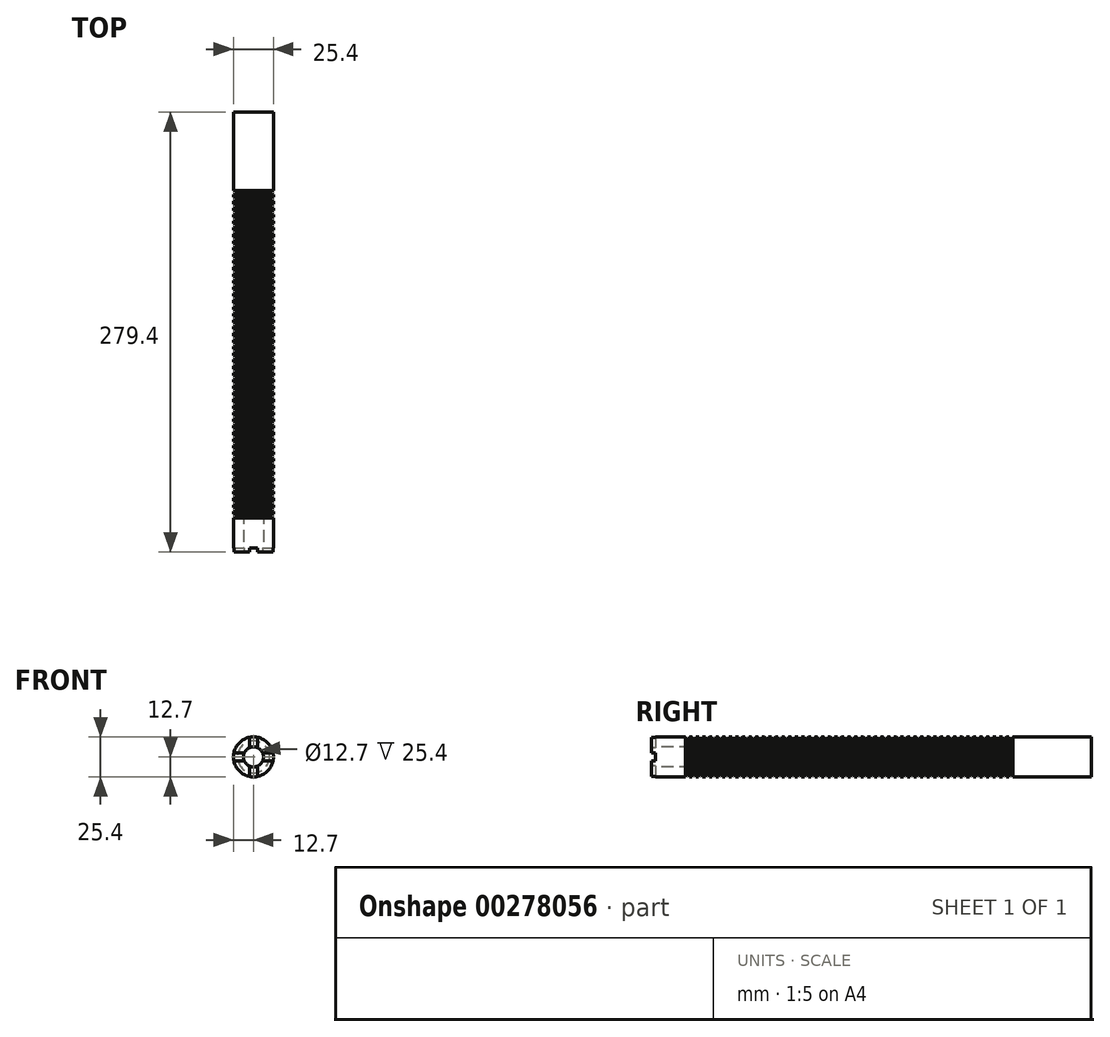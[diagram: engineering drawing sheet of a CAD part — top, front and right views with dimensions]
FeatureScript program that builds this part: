
annotation { "Feature Type Name" : "Feature", "Feature Type Description" : "" }
export const myFeature = defineFeature(function(context is Context, id is Id, definition is map)
    precondition{}
    {
        {
            var Q0;
            Q0=qCreatedBy(makeId("Front.planeOp"),FACE);
            var sketch = newSketch(context, id + "F0", { "sketchPlane" : qUnion([Q0])});
            skCircle(sketch, "E0", {"center": v(0, 0) * mm, "radius": 12.7 * mm});
            skSolve(sketch);
        }
        {
            var Q0;
            Q0 = qSketchRegion(id + "F0", true);
            extrude(context, id + "F1", {"entities" : qUnion([Q0]), "depth" : 279.4 * mm});
        }
        {
            var Q0;
            Q0=makeQuery(id+"F1.opExtrude","CAP_FACE",FACE,{"disambiguationData":[OSD([sQuery(id+"F0.wireOp",EDGE,"E0")])],"isStart":false});
            var sketch = newSketch(context, id + "F2", { "sketchPlane" : qUnion([Q0])});
            skCircle(sketch, "E1", {"center": v(0, 0) * mm, "radius": 6.35 * mm});
            skSolve(sketch);
        }
        {
            var Q0;
            Q0 = qSketchRegion(id + "F2", true);
            extrude(context, id + "F3", {"entities" : qUnion([Q0]), "operationType" : NewBodyOperationType.REMOVE, "oppositeDirection" : true, "depth" : 25.4 * mm});
        }
        {
            var Q0;
            Q0=makeQuery(id+"F1.opExtrude","CAP_FACE",FACE,{"disambiguationData":[OSD([sQuery(id+"F0.wireOp",EDGE,"E0")])],"isStart":false});
            var sketch = newSketch(context, id + "F4", { "sketchPlane" : qUnion([Q0])});
            skLineSegment(sketch, "E2.bottom", {"start": v(-2.54, 19.05) * mm, "end": v(2.54, 19.05) * mm});
            skLineSegment(sketch, "E2.top", {"start": v(-2.54, -19.05) * mm, "end": v(2.54, -19.05) * mm});
            skLineSegment(sketch, "E2.left", {"start": v(-2.54, 19.05) * mm, "end": v(-2.54, -19.05) * mm});
            skLineSegment(sketch, "E2.right", {"start": v(2.54, 19.05) * mm, "end": v(2.54, -19.05) * mm});
            skSolve(sketch);
        }
        {
            var Q0;
            Q0 = qSketchRegion(id + "F4", true);
            extrude(context, id + "F5", {"entities" : qUnion([Q0]), "operationType" : NewBodyOperationType.REMOVE, "oppositeDirection" : true, "depth" : 2.54 * mm});
        }
        {
            var Q0;
            {var subQ0=sQuery(id+"F0.wireOp",EDGE,"E0");Q0=makeQuery(id+"F5.boolean.opBoolean","SPLIT",FACE,{"disambiguationData":[TD([makeQuery(id+"F5.opExtrude","SWEPT_FACE",FACE,{"disambiguationData":[OSD([sQuery(id+"F4.wireOp",EDGE,"E2.left")])]})])],"derivedFrom":makeQuery(id+"F1.opExtrude","CAP_FACE",FACE,{"disambiguationData":[OSD([subQ0])],"isStart":false})});}
            var sketch = newSketch(context, id + "F6", { "sketchPlane" : qUnion([Q0])});
            skLineSegment(sketch, "E3.bottom", {"start": v(-19.05, 2.54) * mm, "end": v(19.05, 2.54) * mm});
            skLineSegment(sketch, "E3.top", {"start": v(-19.05, -2.54) * mm, "end": v(19.05, -2.54) * mm});
            skLineSegment(sketch, "E3.left", {"start": v(-19.05, 2.54) * mm, "end": v(-19.05, -2.54) * mm});
            skLineSegment(sketch, "E3.right", {"start": v(19.05, 2.54) * mm, "end": v(19.05, -2.54) * mm});
            skSolve(sketch);
        }
        {
            var Q0;
            Q0 = qSketchRegion(id + "F6", true);
            extrude(context, id + "F7", {"entities" : qUnion([Q0]), "operationType" : NewBodyOperationType.REMOVE, "oppositeDirection" : true, "depth" : 2.54 * mm});
        }
        {
            var Q0;
            Q0=qCreatedBy(makeId("Right.planeOp"),FACE);
            var sketch = newSketch(context, id + "F8", { "sketchPlane" : qUnion([Q0])});
            skLineSegment(sketch, "E4", {"start": v(-255.27, 12.7) * mm, "end": v(-257.81, 12.7) * mm});
            skLineSegment(sketch, "E5", {"start": v(-257.8, 12.7) * mm, "end": v(-257.18, 10.16) * mm});
            skLineSegment(sketch, "E6", {"start": v(-257.18, 10.16) * mm, "end": v(-255.9, 10.16) * mm});
            skLineSegment(sketch, "E7", {"start": v(-255.9, 10.16) * mm, "end": v(-255.27, 12.7) * mm});
            skLineSegment(sketch, "E8.1.0.0", {"start": v(-251.71, 10.16) * mm, "end": v(-251.08, 12.7) * mm});
            skLineSegment(sketch, "E8.1.0.1", {"start": v(-253.62, 12.7) * mm, "end": v(-252.98, 10.16) * mm});
            skLineSegment(sketch, "E8.1.0.2", {"start": v(-251.08, 12.7) * mm, "end": v(-253.62, 12.7) * mm});
            skLineSegment(sketch, "E8.1.0.3", {"start": v(-252.98, 10.16) * mm, "end": v(-251.71, 10.16) * mm});
            skLineSegment(sketch, "E8.2.0.0", {"start": v(-247.52, 10.16) * mm, "end": v(-246.89, 12.7) * mm});
            skLineSegment(sketch, "E8.2.0.1", {"start": v(-249.43, 12.7) * mm, "end": v(-248.8, 10.16) * mm});
            skLineSegment(sketch, "E8.2.0.2", {"start": v(-246.89, 12.7) * mm, "end": v(-249.43, 12.7) * mm});
            skLineSegment(sketch, "E8.2.0.3", {"start": v(-248.8, 10.16) * mm, "end": v(-247.52, 10.16) * mm});
            skLineSegment(sketch, "E8.3.0.0", {"start": v(-243.33, 10.16) * mm, "end": v(-242.7, 12.7) * mm});
            skLineSegment(sketch, "E8.3.0.1", {"start": v(-245.24, 12.7) * mm, "end": v(-244.6, 10.16) * mm});
            skLineSegment(sketch, "E8.3.0.2", {"start": v(-242.7, 12.7) * mm, "end": v(-245.24, 12.7) * mm});
            skLineSegment(sketch, "E8.3.0.3", {"start": v(-244.6, 10.16) * mm, "end": v(-243.33, 10.16) * mm});
            skLineSegment(sketch, "E8.4.0.0", {"start": v(-239.14, 10.16) * mm, "end": v(-238.5, 12.7) * mm});
            skLineSegment(sketch, "E8.4.0.1", {"start": v(-241.05, 12.7) * mm, "end": v(-240.41, 10.16) * mm});
            skLineSegment(sketch, "E8.4.0.2", {"start": v(-238.5, 12.7) * mm, "end": v(-241.05, 12.7) * mm});
            skLineSegment(sketch, "E8.4.0.3", {"start": v(-240.41, 10.16) * mm, "end": v(-239.14, 10.16) * mm});
            skLineSegment(sketch, "E8.5.0.0", {"start": v(-234.95, 10.16) * mm, "end": v(-234.32, 12.7) * mm});
            skLineSegment(sketch, "E8.5.0.1", {"start": v(-236.85, 12.7) * mm, "end": v(-236.22, 10.16) * mm});
            skLineSegment(sketch, "E8.5.0.2", {"start": v(-234.32, 12.7) * mm, "end": v(-236.86, 12.7) * mm});
            skLineSegment(sketch, "E8.5.0.3", {"start": v(-236.22, 10.16) * mm, "end": v(-234.95, 10.16) * mm});
            skLineSegment(sketch, "E8.6.0.0", {"start": v(-230.76, 10.16) * mm, "end": v(-230.12, 12.7) * mm});
            skLineSegment(sketch, "E8.6.0.1", {"start": v(-232.66, 12.7) * mm, "end": v(-232.03, 10.16) * mm});
            skLineSegment(sketch, "E8.6.0.2", {"start": v(-230.12, 12.7) * mm, "end": v(-232.66, 12.7) * mm});
            skLineSegment(sketch, "E8.6.0.3", {"start": v(-232.03, 10.16) * mm, "end": v(-230.76, 10.16) * mm});
            skLineSegment(sketch, "E8.7.0.0", {"start": v(-226.57, 10.16) * mm, "end": v(-225.93, 12.7) * mm});
            skLineSegment(sketch, "E8.7.0.1", {"start": v(-228.47, 12.7) * mm, "end": v(-227.84, 10.16) * mm});
            skLineSegment(sketch, "E8.7.0.2", {"start": v(-225.93, 12.7) * mm, "end": v(-228.47, 12.7) * mm});
            skLineSegment(sketch, "E8.7.0.3", {"start": v(-227.84, 10.16) * mm, "end": v(-226.57, 10.16) * mm});
            skLineSegment(sketch, "E8.8.0.0", {"start": v(-222.38, 10.16) * mm, "end": v(-221.74, 12.7) * mm});
            skLineSegment(sketch, "E8.8.0.1", {"start": v(-224.28, 12.7) * mm, "end": v(-223.65, 10.16) * mm});
            skLineSegment(sketch, "E8.8.0.2", {"start": v(-221.74, 12.7) * mm, "end": v(-224.28, 12.7) * mm});
            skLineSegment(sketch, "E8.8.0.3", {"start": v(-223.65, 10.16) * mm, "end": v(-222.38, 10.16) * mm});
            skLineSegment(sketch, "E8.9.0.0", {"start": v(-218.19, 10.16) * mm, "end": v(-217.55, 12.7) * mm});
            skLineSegment(sketch, "E8.9.0.1", {"start": v(-220.1, 12.7) * mm, "end": v(-219.46, 10.16) * mm});
            skLineSegment(sketch, "E8.9.0.2", {"start": v(-217.55, 12.7) * mm, "end": v(-220.1, 12.7) * mm});
            skLineSegment(sketch, "E8.9.0.3", {"start": v(-219.46, 10.16) * mm, "end": v(-218.19, 10.16) * mm});
            skLineSegment(sketch, "E8.10.0.0", {"start": v(-214, 10.16) * mm, "end": v(-213.36, 12.7) * mm});
            skLineSegment(sketch, "E8.10.0.1", {"start": v(-215.9, 12.7) * mm, "end": v(-215.26, 10.16) * mm});
            skLineSegment(sketch, "E8.10.0.2", {"start": v(-213.36, 12.7) * mm, "end": v(-215.9, 12.7) * mm});
            skLineSegment(sketch, "E8.10.0.3", {"start": v(-215.27, 10.16) * mm, "end": v(-214, 10.16) * mm});
            skLineSegment(sketch, "E8.11.0.0", {"start": v(-209.8, 10.16) * mm, "end": v(-209.17, 12.7) * mm});
            skLineSegment(sketch, "E8.11.0.1", {"start": v(-211.7, 12.7) * mm, "end": v(-211.07, 10.16) * mm});
            skLineSegment(sketch, "E8.11.0.2", {"start": v(-209.17, 12.7) * mm, "end": v(-211.7, 12.7) * mm});
            skLineSegment(sketch, "E8.11.0.3", {"start": v(-211.07, 10.16) * mm, "end": v(-209.8, 10.16) * mm});
            skLineSegment(sketch, "E8.12.0.0", {"start": v(-205.61, 10.16) * mm, "end": v(-204.98, 12.7) * mm});
            skLineSegment(sketch, "E8.12.0.1", {"start": v(-207.52, 12.7) * mm, "end": v(-206.88, 10.16) * mm});
            skLineSegment(sketch, "E8.12.0.2", {"start": v(-204.98, 12.7) * mm, "end": v(-207.52, 12.7) * mm});
            skLineSegment(sketch, "E8.12.0.3", {"start": v(-206.88, 10.16) * mm, "end": v(-205.61, 10.16) * mm});
            skLineSegment(sketch, "E8.13.0.0", {"start": v(-201.42, 10.16) * mm, "end": v(-200.79, 12.7) * mm});
            skLineSegment(sketch, "E8.13.0.1", {"start": v(-203.33, 12.7) * mm, "end": v(-202.7, 10.16) * mm});
            skLineSegment(sketch, "E8.13.0.2", {"start": v(-200.79, 12.7) * mm, "end": v(-203.33, 12.7) * mm});
            skLineSegment(sketch, "E8.13.0.3", {"start": v(-202.7, 10.16) * mm, "end": v(-201.42, 10.16) * mm});
            skLineSegment(sketch, "E8.14.0.0", {"start": v(-197.23, 10.16) * mm, "end": v(-196.6, 12.7) * mm});
            skLineSegment(sketch, "E8.14.0.1", {"start": v(-199.14, 12.7) * mm, "end": v(-198.5, 10.16) * mm});
            skLineSegment(sketch, "E8.14.0.2", {"start": v(-196.6, 12.7) * mm, "end": v(-199.14, 12.7) * mm});
            skLineSegment(sketch, "E8.14.0.3", {"start": v(-198.5, 10.16) * mm, "end": v(-197.23, 10.16) * mm});
            skLineSegment(sketch, "E8.15.0.0", {"start": v(-193.04, 10.16) * mm, "end": v(-192.4, 12.7) * mm});
            skLineSegment(sketch, "E8.15.0.1", {"start": v(-194.94, 12.7) * mm, "end": v(-194.3, 10.16) * mm});
            skLineSegment(sketch, "E8.15.0.2", {"start": v(-192.4, 12.7) * mm, "end": v(-194.95, 12.7) * mm});
            skLineSegment(sketch, "E8.15.0.3", {"start": v(-194.31, 10.16) * mm, "end": v(-193.04, 10.16) * mm});
            skLineSegment(sketch, "E8.16.0.0", {"start": v(-188.85, 10.16) * mm, "end": v(-188.21, 12.7) * mm});
            skLineSegment(sketch, "E8.16.0.1", {"start": v(-190.75, 12.7) * mm, "end": v(-190.12, 10.16) * mm});
            skLineSegment(sketch, "E8.16.0.2", {"start": v(-188.21, 12.7) * mm, "end": v(-190.75, 12.7) * mm});
            skLineSegment(sketch, "E8.16.0.3", {"start": v(-190.12, 10.16) * mm, "end": v(-188.85, 10.16) * mm});
            skLineSegment(sketch, "E8.17.0.0", {"start": v(-184.66, 10.16) * mm, "end": v(-184.02, 12.7) * mm});
            skLineSegment(sketch, "E8.17.0.1", {"start": v(-186.56, 12.7) * mm, "end": v(-185.93, 10.16) * mm});
            skLineSegment(sketch, "E8.17.0.2", {"start": v(-184.02, 12.7) * mm, "end": v(-186.56, 12.7) * mm});
            skLineSegment(sketch, "E8.17.0.3", {"start": v(-185.93, 10.16) * mm, "end": v(-184.66, 10.16) * mm});
            skLineSegment(sketch, "E8.18.0.0", {"start": v(-180.47, 10.16) * mm, "end": v(-179.83, 12.7) * mm});
            skLineSegment(sketch, "E8.18.0.1", {"start": v(-182.37, 12.7) * mm, "end": v(-181.74, 10.16) * mm});
            skLineSegment(sketch, "E8.18.0.2", {"start": v(-179.83, 12.7) * mm, "end": v(-182.37, 12.7) * mm});
            skLineSegment(sketch, "E8.18.0.3", {"start": v(-181.74, 10.16) * mm, "end": v(-180.47, 10.16) * mm});
            skLineSegment(sketch, "E8.19.0.0", {"start": v(-176.28, 10.16) * mm, "end": v(-175.64, 12.7) * mm});
            skLineSegment(sketch, "E8.19.0.1", {"start": v(-178.18, 12.7) * mm, "end": v(-177.55, 10.16) * mm});
            skLineSegment(sketch, "E8.19.0.2", {"start": v(-175.64, 12.7) * mm, "end": v(-178.18, 12.7) * mm});
            skLineSegment(sketch, "E8.19.0.3", {"start": v(-177.55, 10.16) * mm, "end": v(-176.28, 10.16) * mm});
            skLineSegment(sketch, "E8.20.0.0", {"start": v(-172.09, 10.16) * mm, "end": v(-171.45, 12.7) * mm});
            skLineSegment(sketch, "E8.20.0.1", {"start": v(-173.99, 12.7) * mm, "end": v(-173.35, 10.16) * mm});
            skLineSegment(sketch, "E8.20.0.2", {"start": v(-171.45, 12.7) * mm, "end": v(-174, 12.7) * mm});
            skLineSegment(sketch, "E8.20.0.3", {"start": v(-173.36, 10.16) * mm, "end": v(-172.09, 10.16) * mm});
            skLineSegment(sketch, "E8.21.0.0", {"start": v(-167.9, 10.16) * mm, "end": v(-167.26, 12.7) * mm});
            skLineSegment(sketch, "E8.21.0.1", {"start": v(-169.8, 12.7) * mm, "end": v(-169.16, 10.16) * mm});
            skLineSegment(sketch, "E8.21.0.2", {"start": v(-167.26, 12.7) * mm, "end": v(-169.8, 12.7) * mm});
            skLineSegment(sketch, "E8.21.0.3", {"start": v(-169.16, 10.16) * mm, "end": v(-167.9, 10.16) * mm});
            skLineSegment(sketch, "E8.22.0.0", {"start": v(-163.7, 10.16) * mm, "end": v(-163.07, 12.7) * mm});
            skLineSegment(sketch, "E8.22.0.1", {"start": v(-165.6, 12.7) * mm, "end": v(-164.97, 10.16) * mm});
            skLineSegment(sketch, "E8.22.0.2", {"start": v(-163.07, 12.7) * mm, "end": v(-165.6, 12.7) * mm});
            skLineSegment(sketch, "E8.22.0.3", {"start": v(-164.97, 10.16) * mm, "end": v(-163.7, 10.16) * mm});
            skLineSegment(sketch, "E8.23.0.0", {"start": v(-159.51, 10.16) * mm, "end": v(-158.88, 12.7) * mm});
            skLineSegment(sketch, "E8.23.0.1", {"start": v(-161.42, 12.7) * mm, "end": v(-160.78, 10.16) * mm});
            skLineSegment(sketch, "E8.23.0.2", {"start": v(-158.88, 12.7) * mm, "end": v(-161.42, 12.7) * mm});
            skLineSegment(sketch, "E8.23.0.3", {"start": v(-160.78, 10.16) * mm, "end": v(-159.51, 10.16) * mm});
            skLineSegment(sketch, "E8.24.0.0", {"start": v(-155.32, 10.16) * mm, "end": v(-154.69, 12.7) * mm});
            skLineSegment(sketch, "E8.24.0.1", {"start": v(-157.23, 12.7) * mm, "end": v(-156.6, 10.16) * mm});
            skLineSegment(sketch, "E8.24.0.2", {"start": v(-154.69, 12.7) * mm, "end": v(-157.23, 12.7) * mm});
            skLineSegment(sketch, "E8.24.0.3", {"start": v(-156.6, 10.16) * mm, "end": v(-155.32, 10.16) * mm});
            skLineSegment(sketch, "E8.25.0.0", {"start": v(-151.13, 10.16) * mm, "end": v(-150.5, 12.7) * mm});
            skLineSegment(sketch, "E8.25.0.1", {"start": v(-153.03, 12.7) * mm, "end": v(-152.4, 10.16) * mm});
            skLineSegment(sketch, "E8.25.0.2", {"start": v(-150.5, 12.7) * mm, "end": v(-153.04, 12.7) * mm});
            skLineSegment(sketch, "E8.25.0.3", {"start": v(-152.4, 10.16) * mm, "end": v(-151.13, 10.16) * mm});
            skLineSegment(sketch, "E8.26.0.0", {"start": v(-146.94, 10.16) * mm, "end": v(-146.3, 12.7) * mm});
            skLineSegment(sketch, "E8.26.0.1", {"start": v(-148.84, 12.7) * mm, "end": v(-148.2, 10.16) * mm});
            skLineSegment(sketch, "E8.26.0.2", {"start": v(-146.3, 12.7) * mm, "end": v(-148.84, 12.7) * mm});
            skLineSegment(sketch, "E8.26.0.3", {"start": v(-148.2, 10.16) * mm, "end": v(-146.94, 10.16) * mm});
            skLineSegment(sketch, "E8.27.0.0", {"start": v(-142.75, 10.16) * mm, "end": v(-142.11, 12.7) * mm});
            skLineSegment(sketch, "E8.27.0.1", {"start": v(-144.65, 12.7) * mm, "end": v(-144.02, 10.16) * mm});
            skLineSegment(sketch, "E8.27.0.2", {"start": v(-142.11, 12.7) * mm, "end": v(-144.65, 12.7) * mm});
            skLineSegment(sketch, "E8.27.0.3", {"start": v(-144.02, 10.16) * mm, "end": v(-142.75, 10.16) * mm});
            skLineSegment(sketch, "E8.28.0.0", {"start": v(-138.56, 10.16) * mm, "end": v(-137.92, 12.7) * mm});
            skLineSegment(sketch, "E8.28.0.1", {"start": v(-140.46, 12.7) * mm, "end": v(-139.83, 10.16) * mm});
            skLineSegment(sketch, "E8.28.0.2", {"start": v(-137.92, 12.7) * mm, "end": v(-140.46, 12.7) * mm});
            skLineSegment(sketch, "E8.28.0.3", {"start": v(-139.83, 10.16) * mm, "end": v(-138.56, 10.16) * mm});
            skLineSegment(sketch, "E8.29.0.0", {"start": v(-134.37, 10.16) * mm, "end": v(-133.73, 12.7) * mm});
            skLineSegment(sketch, "E8.29.0.1", {"start": v(-136.27, 12.7) * mm, "end": v(-135.64, 10.16) * mm});
            skLineSegment(sketch, "E8.29.0.2", {"start": v(-133.73, 12.7) * mm, "end": v(-136.27, 12.7) * mm});
            skLineSegment(sketch, "E8.29.0.3", {"start": v(-135.64, 10.16) * mm, "end": v(-134.37, 10.16) * mm});
            skLineSegment(sketch, "E8.30.0.0", {"start": v(-130.18, 10.16) * mm, "end": v(-129.54, 12.7) * mm});
            skLineSegment(sketch, "E8.30.0.1", {"start": v(-132.08, 12.7) * mm, "end": v(-131.44, 10.16) * mm});
            skLineSegment(sketch, "E8.30.0.2", {"start": v(-129.54, 12.7) * mm, "end": v(-132.08, 12.7) * mm});
            skLineSegment(sketch, "E8.30.0.3", {"start": v(-131.45, 10.16) * mm, "end": v(-130.18, 10.16) * mm});
            skLineSegment(sketch, "E8.31.0.0", {"start": v(-125.98, 10.16) * mm, "end": v(-125.35, 12.7) * mm});
            skLineSegment(sketch, "E8.31.0.1", {"start": v(-127.89, 12.7) * mm, "end": v(-127.25, 10.16) * mm});
            skLineSegment(sketch, "E8.31.0.2", {"start": v(-125.35, 12.7) * mm, "end": v(-127.89, 12.7) * mm});
            skLineSegment(sketch, "E8.31.0.3", {"start": v(-127.25, 10.16) * mm, "end": v(-125.98, 10.16) * mm});
            skLineSegment(sketch, "E8.32.0.0", {"start": v(-121.8, 10.16) * mm, "end": v(-121.16, 12.7) * mm});
            skLineSegment(sketch, "E8.32.0.1", {"start": v(-123.7, 12.7) * mm, "end": v(-123.06, 10.16) * mm});
            skLineSegment(sketch, "E8.32.0.2", {"start": v(-121.16, 12.7) * mm, "end": v(-123.7, 12.7) * mm});
            skLineSegment(sketch, "E8.32.0.3", {"start": v(-123.06, 10.16) * mm, "end": v(-121.8, 10.16) * mm});
            skLineSegment(sketch, "E8.33.0.0", {"start": v(-117.6, 10.16) * mm, "end": v(-116.97, 12.7) * mm});
            skLineSegment(sketch, "E8.33.0.1", {"start": v(-119.5, 12.7) * mm, "end": v(-118.87, 10.16) * mm});
            skLineSegment(sketch, "E8.33.0.2", {"start": v(-116.97, 12.7) * mm, "end": v(-119.5, 12.7) * mm});
            skLineSegment(sketch, "E8.33.0.3", {"start": v(-118.87, 10.16) * mm, "end": v(-117.6, 10.16) * mm});
            skLineSegment(sketch, "E8.34.0.0", {"start": v(-113.41, 10.16) * mm, "end": v(-112.78, 12.7) * mm});
            skLineSegment(sketch, "E8.34.0.1", {"start": v(-115.32, 12.7) * mm, "end": v(-114.68, 10.16) * mm});
            skLineSegment(sketch, "E8.34.0.2", {"start": v(-112.78, 12.7) * mm, "end": v(-115.32, 12.7) * mm});
            skLineSegment(sketch, "E8.34.0.3", {"start": v(-114.68, 10.16) * mm, "end": v(-113.41, 10.16) * mm});
            skLineSegment(sketch, "E8.35.0.0", {"start": v(-109.22, 10.16) * mm, "end": v(-108.59, 12.7) * mm});
            skLineSegment(sketch, "E8.35.0.1", {"start": v(-111.12, 12.7) * mm, "end": v(-110.49, 10.16) * mm});
            skLineSegment(sketch, "E8.35.0.2", {"start": v(-108.59, 12.7) * mm, "end": v(-111.13, 12.7) * mm});
            skLineSegment(sketch, "E8.35.0.3", {"start": v(-110.5, 10.16) * mm, "end": v(-109.22, 10.16) * mm});
            skLineSegment(sketch, "E8.36.0.0", {"start": v(-105.03, 10.16) * mm, "end": v(-104.4, 12.7) * mm});
            skLineSegment(sketch, "E8.36.0.1", {"start": v(-106.93, 12.7) * mm, "end": v(-106.3, 10.16) * mm});
            skLineSegment(sketch, "E8.36.0.2", {"start": v(-104.4, 12.7) * mm, "end": v(-106.93, 12.7) * mm});
            skLineSegment(sketch, "E8.36.0.3", {"start": v(-106.3, 10.16) * mm, "end": v(-105.03, 10.16) * mm});
            skLineSegment(sketch, "E8.37.0.0", {"start": v(-100.84, 10.16) * mm, "end": v(-100.2, 12.7) * mm});
            skLineSegment(sketch, "E8.37.0.1", {"start": v(-102.74, 12.7) * mm, "end": v(-102.1, 10.16) * mm});
            skLineSegment(sketch, "E8.37.0.2", {"start": v(-100.2, 12.7) * mm, "end": v(-102.74, 12.7) * mm});
            skLineSegment(sketch, "E8.37.0.3", {"start": v(-102.1, 10.16) * mm, "end": v(-100.84, 10.16) * mm});
            skLineSegment(sketch, "E8.38.0.0", {"start": v(-96.65, 10.16) * mm, "end": v(-96.01, 12.7) * mm});
            skLineSegment(sketch, "E8.38.0.1", {"start": v(-98.55, 12.7) * mm, "end": v(-97.92, 10.16) * mm});
            skLineSegment(sketch, "E8.38.0.2", {"start": v(-96.01, 12.7) * mm, "end": v(-98.55, 12.7) * mm});
            skLineSegment(sketch, "E8.38.0.3", {"start": v(-97.92, 10.16) * mm, "end": v(-96.65, 10.16) * mm});
            skLineSegment(sketch, "E8.39.0.0", {"start": v(-92.46, 10.16) * mm, "end": v(-91.82, 12.7) * mm});
            skLineSegment(sketch, "E8.39.0.1", {"start": v(-94.36, 12.7) * mm, "end": v(-93.73, 10.16) * mm});
            skLineSegment(sketch, "E8.39.0.2", {"start": v(-91.82, 12.7) * mm, "end": v(-94.36, 12.7) * mm});
            skLineSegment(sketch, "E8.39.0.3", {"start": v(-93.73, 10.16) * mm, "end": v(-92.46, 10.16) * mm});
            skLineSegment(sketch, "E8.40.0.0", {"start": v(-88.27, 10.16) * mm, "end": v(-87.63, 12.7) * mm});
            skLineSegment(sketch, "E8.40.0.1", {"start": v(-90.17, 12.7) * mm, "end": v(-89.53, 10.16) * mm});
            skLineSegment(sketch, "E8.40.0.2", {"start": v(-87.63, 12.7) * mm, "end": v(-90.17, 12.7) * mm});
            skLineSegment(sketch, "E8.40.0.3", {"start": v(-89.54, 10.16) * mm, "end": v(-88.27, 10.16) * mm});
            skLineSegment(sketch, "E8.41.0.0", {"start": v(-84.07, 10.16) * mm, "end": v(-83.44, 12.7) * mm});
            skLineSegment(sketch, "E8.41.0.1", {"start": v(-85.98, 12.7) * mm, "end": v(-85.34, 10.16) * mm});
            skLineSegment(sketch, "E8.41.0.2", {"start": v(-83.44, 12.7) * mm, "end": v(-85.98, 12.7) * mm});
            skLineSegment(sketch, "E8.41.0.3", {"start": v(-85.34, 10.16) * mm, "end": v(-84.07, 10.16) * mm});
            skLineSegment(sketch, "E8.42.0.0", {"start": v(-79.88, 10.16) * mm, "end": v(-79.25, 12.7) * mm});
            skLineSegment(sketch, "E8.42.0.1", {"start": v(-81.79, 12.7) * mm, "end": v(-81.15, 10.16) * mm});
            skLineSegment(sketch, "E8.42.0.2", {"start": v(-79.25, 12.7) * mm, "end": v(-81.79, 12.7) * mm});
            skLineSegment(sketch, "E8.42.0.3", {"start": v(-81.15, 10.16) * mm, "end": v(-79.88, 10.16) * mm});
            skLineSegment(sketch, "E8.43.0.0", {"start": v(-75.7, 10.16) * mm, "end": v(-75.06, 12.7) * mm});
            skLineSegment(sketch, "E8.43.0.1", {"start": v(-77.6, 12.7) * mm, "end": v(-76.96, 10.16) * mm});
            skLineSegment(sketch, "E8.43.0.2", {"start": v(-75.06, 12.7) * mm, "end": v(-77.6, 12.7) * mm});
            skLineSegment(sketch, "E8.43.0.3", {"start": v(-76.96, 10.16) * mm, "end": v(-75.7, 10.16) * mm});
            skLineSegment(sketch, "E8.44.0.0", {"start": v(-71.5, 10.16) * mm, "end": v(-70.87, 12.7) * mm});
            skLineSegment(sketch, "E8.44.0.1", {"start": v(-73.4, 12.7) * mm, "end": v(-72.77, 10.16) * mm});
            skLineSegment(sketch, "E8.44.0.2", {"start": v(-70.87, 12.7) * mm, "end": v(-73.4, 12.7) * mm});
            skLineSegment(sketch, "E8.44.0.3", {"start": v(-72.77, 10.16) * mm, "end": v(-71.5, 10.16) * mm});
            skLineSegment(sketch, "E8.45.0.0", {"start": v(-67.3, 10.16) * mm, "end": v(-66.67, 12.7) * mm});
            skLineSegment(sketch, "E8.45.0.1", {"start": v(-69.21, 12.7) * mm, "end": v(-68.58, 10.16) * mm});
            skLineSegment(sketch, "E8.45.0.2", {"start": v(-66.68, 12.7) * mm, "end": v(-69.22, 12.7) * mm});
            skLineSegment(sketch, "E8.45.0.3", {"start": v(-68.58, 10.16) * mm, "end": v(-67.31, 10.16) * mm});
            skLineSegment(sketch, "E8.46.0.0", {"start": v(-63.12, 10.16) * mm, "end": v(-62.48, 12.7) * mm});
            skLineSegment(sketch, "E8.46.0.1", {"start": v(-65.02, 12.7) * mm, "end": v(-64.39, 10.16) * mm});
            skLineSegment(sketch, "E8.46.0.2", {"start": v(-62.48, 12.7) * mm, "end": v(-65.02, 12.7) * mm});
            skLineSegment(sketch, "E8.46.0.3", {"start": v(-64.39, 10.16) * mm, "end": v(-63.12, 10.16) * mm});
            skLineSegment(sketch, "E8.47.0.0", {"start": v(-58.93, 10.16) * mm, "end": v(-58.3, 12.7) * mm});
            skLineSegment(sketch, "E8.47.0.1", {"start": v(-60.83, 12.7) * mm, "end": v(-60.2, 10.16) * mm});
            skLineSegment(sketch, "E8.47.0.2", {"start": v(-58.3, 12.7) * mm, "end": v(-60.83, 12.7) * mm});
            skLineSegment(sketch, "E8.47.0.3", {"start": v(-60.2, 10.16) * mm, "end": v(-58.93, 10.16) * mm});
            skLineSegment(sketch, "E8.48.0.0", {"start": v(-54.74, 10.16) * mm, "end": v(-54.1, 12.7) * mm});
            skLineSegment(sketch, "E8.48.0.1", {"start": v(-56.64, 12.7) * mm, "end": v(-56, 10.16) * mm});
            skLineSegment(sketch, "E8.48.0.2", {"start": v(-54.1, 12.7) * mm, "end": v(-56.64, 12.7) * mm});
            skLineSegment(sketch, "E8.48.0.3", {"start": v(-56, 10.16) * mm, "end": v(-54.74, 10.16) * mm});
            skLineSegment(sketch, "E8.49.0.0", {"start": v(-50.55, 10.16) * mm, "end": v(-49.91, 12.7) * mm});
            skLineSegment(sketch, "E8.49.0.1", {"start": v(-52.45, 12.7) * mm, "end": v(-51.82, 10.16) * mm});
            skLineSegment(sketch, "E8.49.0.2", {"start": v(-49.91, 12.7) * mm, "end": v(-52.45, 12.7) * mm});
            skLineSegment(sketch, "E8.49.0.3", {"start": v(-51.82, 10.16) * mm, "end": v(-50.55, 10.16) * mm});
            skLineSegment(sketch, "E8.direction1", {"start": v(-257.18, 10.16) * mm, "end": v(-252.98, 10.16) * mm, "construction": true});
            skSolve(sketch);
        }
        {
            var Q0;
            Q0 = qSketchRegion(id + "F8", true);
            var Q1;
            Q1=makeQuery(id+"F1.opExtrude","SWEPT_FACE",FACE,{"disambiguationData":[OSD([sQuery(id+"F0.wireOp",EDGE,"E0")])]});
            revolve(context, id + "F9", {"operationType" : NewBodyOperationType.REMOVE, "entities" : qUnion([Q0]), "axis" : qUnion([Q1]), "revolveType" : RevolveType.FULL, "oppositeDirection" : true});
        }
    });
